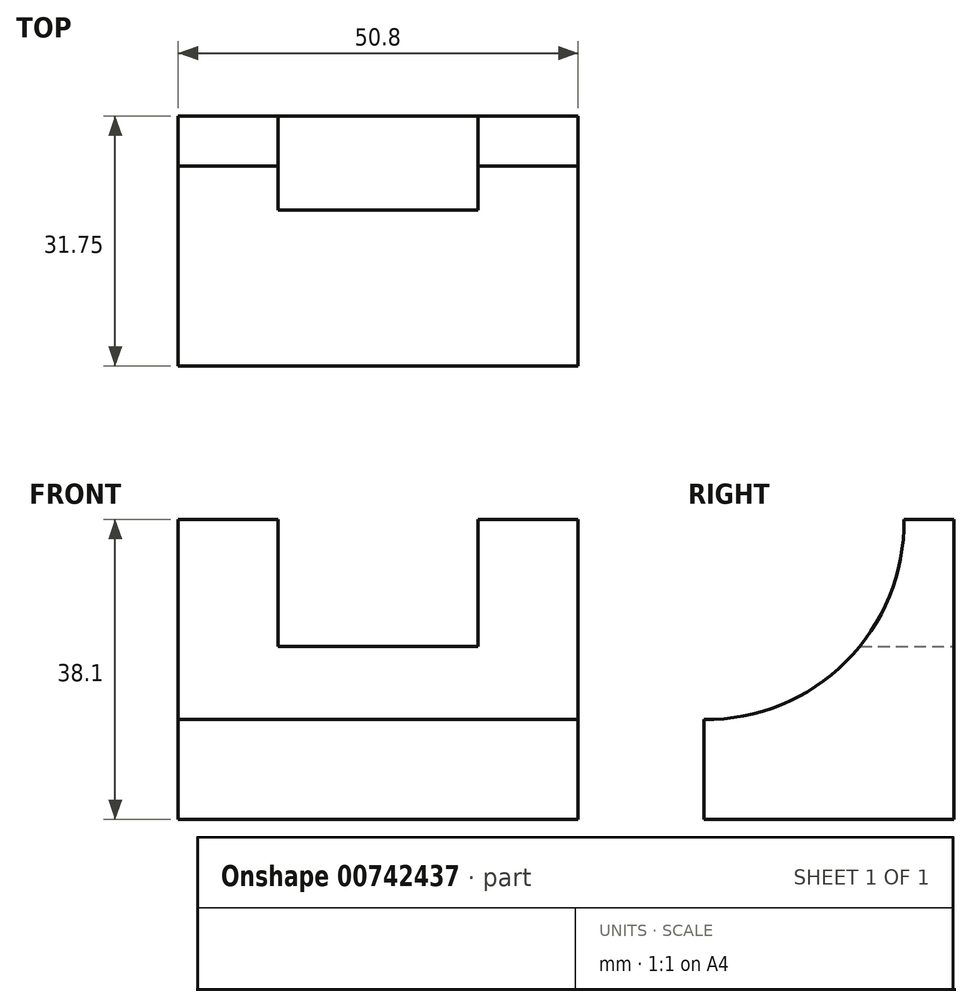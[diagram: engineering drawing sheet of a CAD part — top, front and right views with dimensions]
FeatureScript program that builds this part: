
annotation { "Feature Type Name" : "Feature", "Feature Type Description" : "" }
export const myFeature = defineFeature(function(context is Context, id is Id, definition is map)
    precondition{}
    {
        {
            var Q0;
            Q0=qCreatedBy(makeId("Front.planeOp"),FACE);
            var sketch = newSketch(context, id + "F0", { "sketchPlane" : qUnion([Q0])});
            skLineSegment(sketch, "E0", {"start": v(0, 0) * mm, "end": v(0, 38.1) * mm});
            skLineSegment(sketch, "E1", {"start": v(0, 38.1) * mm, "end": v(50.8, 38.1) * mm});
            skLineSegment(sketch, "E2", {"start": v(50.8, 38.1) * mm, "end": v(50.8, 0) * mm});
            skLineSegment(sketch, "E3", {"start": v(50.8, 0) * mm, "end": v(0, 0) * mm});
            skSolve(sketch);
        }
        {
            var Q0;
            Q0 = qSketchRegion(id + "F0", true);
            extrude(context, id + "F1", {"entities" : qUnion([Q0]), "depth" : 31.75 * mm, "offsetDistance" : 25.4 * mm});
        }
        {
            var Q0;
            Q0=makeQuery(id+"F1.opExtrude","CAP_FACE",FACE,{"disambiguationData":[OSD([sQuery(id+"F0.wireOp",EDGE,"E0"),sQuery(id+"F0.wireOp",EDGE,"E1"),sQuery(id+"F0.wireOp",EDGE,"E2"),sQuery(id+"F0.wireOp",EDGE,"E3")])],"isStart":true});
            var sketch = newSketch(context, id + "F2", { "sketchPlane" : qUnion([Q0])});
            skLineSegment(sketch, "E4", {"start": v(-38.1, 38.1) * mm, "end": v(-38.1, 21.99) * mm});
            skLineSegment(sketch, "E5", {"start": v(-38.1, 21.99) * mm, "end": v(-12.7, 21.99) * mm});
            skLineSegment(sketch, "E6", {"start": v(-12.7, 21.99) * mm, "end": v(-12.7, 38.1) * mm});
            skSolve(sketch);
        }
        {
            var Q0;
            {var subQ0=sQuery(id+"F2.wireOp",EDGE,"E4");Q0=makeQuery(id+"F2.imprint","IMPRINT",FACE,{"disambiguationData":[TD([[makeQuery(id+"F2.imprint","IMPRINT",EDGE,{"derivedFrom":subQ0}),1.0]])]});}
            extrude(context, id + "F3", {"entities" : qUnion([Q0]), "operationType" : NewBodyOperationType.REMOVE, "oppositeDirection" : true, "depth" : 12.7 * mm, "offsetDistance" : 25.4 * mm});
        }
        {
            var Q0;
            Q0=makeQuery(id+"F1.opExtrude","SWEPT_FACE",FACE,{"disambiguationData":[OSD([sQuery(id+"F0.wireOp",EDGE,"E2")])]});
            var sketch = newSketch(context, id + "F4", { "sketchPlane" : qUnion([Q0])});
            skArc(sketch, "E7", {"start": v(-31.75, 12.7) * mm, "mid": v(-13.7, 20.05) * mm, "end": v(-6.35, 38.1) * mm});
            skSolve(sketch);
        }
        {
            var Q0;
            {var subQ0=sQuery(id+"F4.wireOp",EDGE,"E7");Q0=makeQuery(id+"F4.imprint","IMPRINT",FACE,{"disambiguationData":[TD([[makeQuery(id+"F4.imprint","IMPRINT",EDGE,{"derivedFrom":subQ0}),1.0]])]});}
            extrude(context, id + "F5", {"entities" : qUnion([Q0]), "operationType" : NewBodyOperationType.REMOVE, "endBound" : BoundingType.THROUGH_ALL, "oppositeDirection" : true, "depth" : 25.4 * mm, "offsetDistance" : 25.4 * mm});
        }
    });
